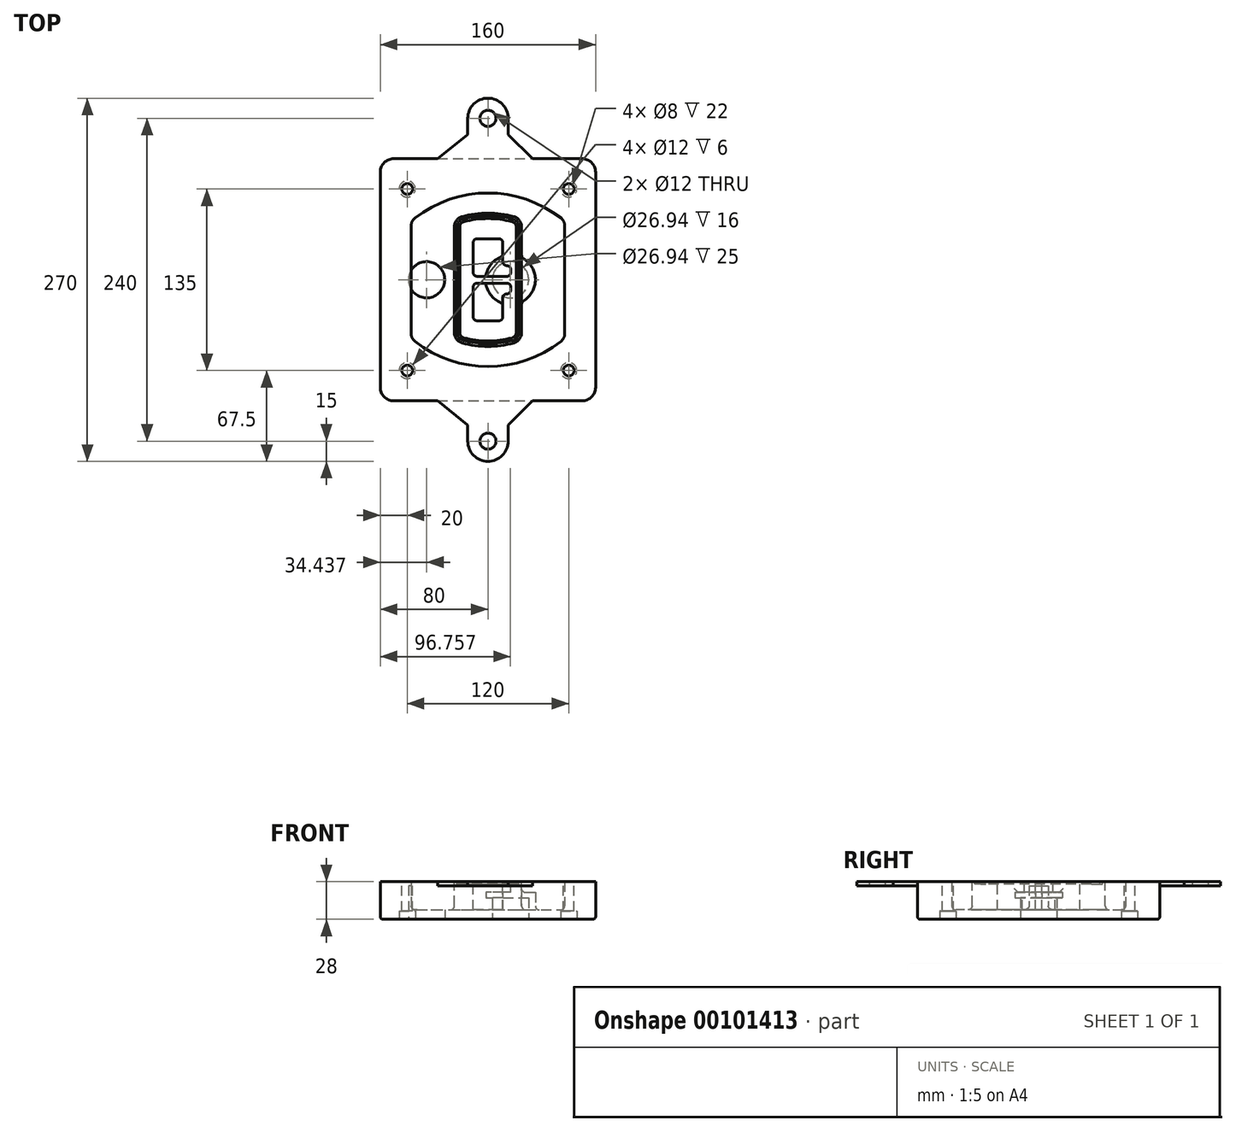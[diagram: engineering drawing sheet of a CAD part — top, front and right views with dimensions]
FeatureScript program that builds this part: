
annotation { "Feature Type Name" : "Feature", "Feature Type Description" : "" }
export const myFeature = defineFeature(function(context is Context, id is Id, definition is map)
    precondition{}
    {
        {
            var Q0;
            Q0=qCreatedBy(makeId("Top.planeOp"),FACE);
            var sketch = newSketch(context, id + "F0", { "sketchPlane" : qUnion([Q0])});
            skPoint(sketch, "E0.rect.middle", {"position": v(0, 0) * mm});
            skLineSegment(sketch, "E1.bottom", {"start": v(-70, -90) * mm, "end": v(70, -90) * mm});
            skLineSegment(sketch, "E1.top", {"start": v(-70, 90) * mm, "end": v(70, 90) * mm});
            skLineSegment(sketch, "E1.left", {"start": v(-80, -80) * mm, "end": v(-80, 80) * mm});
            skLineSegment(sketch, "E1.right", {"start": v(80, -80) * mm, "end": v(80, 80) * mm});
            skLineSegment(sketch, "E2", {"start": v(-80, 90) * mm, "end": v(80, -90) * mm, "construction": true});
            skLineSegment(sketch, "E3", {"start": v(80, 90) * mm, "end": v(-80, -90) * mm, "construction": true});
            skCircle(sketch, "E4", {"center": v(-60, 67.5) * mm, "radius": 4 * mm});
            skCircle(sketch, "E5", {"center": v(60, 67.5) * mm, "radius": 4 * mm});
            skCircle(sketch, "E6", {"center": v(60, -67.5) * mm, "radius": 4 * mm});
            skCircle(sketch, "E7", {"center": v(-60, -67.5) * mm, "radius": 4 * mm});
            skLineSegment(sketch, "E8", {"start": v(-60, 67.5) * mm, "end": v(60, 67.5) * mm, "construction": true});
            skLineSegment(sketch, "E9", {"start": v(60, 67.5) * mm, "end": v(60, -67.5) * mm, "construction": true});
            skLineSegment(sketch, "E10", {"start": v(60, -67.5) * mm, "end": v(-60, -67.5) * mm, "construction": true});
            skLineSegment(sketch, "E11", {"start": v(-60, -67.5) * mm, "end": v(-60, 67.5) * mm, "construction": true});
            skLineSegment(sketch, "E12", {"start": v(-60, 40.3) * mm, "end": v(-60, -40.3) * mm});
            skLineSegment(sketch, "E13", {"start": v(60, 40.3) * mm, "end": v(60, -40.3) * mm});
            skArc(sketch, "E14", {"start": v(56.15, 48.18) * mm, "mid": v(0, 67.5) * mm, "end": v(-56.15, 48.18) * mm});
            skArc(sketch, "E15", {"start": v(-56.15, -48.18) * mm, "mid": v(0, -67.5) * mm, "end": v(56.15, -48.18) * mm});
            skLineSegment(sketch, "E16", {"start": v(-60, 0) * mm, "end": v(60, 0) * mm, "construction": true});
            skPoint(sketch, "E17.visualSharp", {"position": v(-60, -45) * mm});
            skArc(sketch, "E17.filletArc", {"start": v(-60, -40.3) * mm, "mid": v(-58.99, -44.68) * mm, "end": v(-56.15, -48.18) * mm});
            skPoint(sketch, "E18.visualSharp", {"position": v(-60, 45) * mm});
            skArc(sketch, "E18.filletArc", {"start": v(-56.15, 48.18) * mm, "mid": v(-58.99, 44.68) * mm, "end": v(-60, 40.3) * mm});
            skPoint(sketch, "E19.visualSharp", {"position": v(60, 45) * mm});
            skArc(sketch, "E19.filletArc", {"start": v(60, 40.3) * mm, "mid": v(58.99, 44.68) * mm, "end": v(56.15, 48.18) * mm});
            skPoint(sketch, "E20.visualSharp", {"position": v(60, -45) * mm});
            skArc(sketch, "E20.filletArc", {"start": v(56.15, -48.18) * mm, "mid": v(58.99, -44.68) * mm, "end": v(60, -40.3) * mm});
            skPoint(sketch, "E21.visualSharp", {"position": v(-80, 90) * mm});
            skArc(sketch, "E21.filletArc", {"start": v(-70, 90) * mm, "mid": v(-77.07, 87.07) * mm, "end": v(-80, 80) * mm});
            skPoint(sketch, "E22.visualSharp", {"position": v(80, 90) * mm});
            skArc(sketch, "E22.filletArc", {"start": v(80, 80) * mm, "mid": v(77.07, 87.07) * mm, "end": v(70, 90) * mm});
            skPoint(sketch, "E23.visualSharp", {"position": v(80, -90) * mm});
            skArc(sketch, "E23.filletArc", {"start": v(70, -90) * mm, "mid": v(77.07, -87.07) * mm, "end": v(80, -80) * mm});
            skPoint(sketch, "E24.visualSharp", {"position": v(-80, -90) * mm});
            skArc(sketch, "E24.filletArc", {"start": v(-80, -80) * mm, "mid": v(-77.07, -87.07) * mm, "end": v(-70, -90) * mm});
            skArc(sketch, "E25.0", {"start": v(57, 40.3) * mm, "mid": v(56.3, 43.36) * mm, "end": v(54.3, 45.81) * mm});
            skLineSegment(sketch, "E25.1", {"start": v(57, 40.3) * mm, "end": v(57, -40.3) * mm});
            skArc(sketch, "E25.2", {"start": v(54.3, -45.81) * mm, "mid": v(56.3, -43.36) * mm, "end": v(57, -40.3) * mm});
            skArc(sketch, "E25.3", {"start": v(-54.3, -45.81) * mm, "mid": v(0, -64.5) * mm, "end": v(54.3, -45.81) * mm});
            skArc(sketch, "E25.4", {"start": v(-57, -40.3) * mm, "mid": v(-56.3, -43.36) * mm, "end": v(-54.3, -45.81) * mm});
            skArc(sketch, "E25.5", {"start": v(54.3, 45.81) * mm, "mid": v(0, 64.5) * mm, "end": v(-54.3, 45.81) * mm});
            skLineSegment(sketch, "E25.6", {"start": v(-57, 40.3) * mm, "end": v(-57, -40.3) * mm});
            skArc(sketch, "E25.7", {"start": v(-54.3, 45.81) * mm, "mid": v(-56.3, 43.36) * mm, "end": v(-57, 40.3) * mm});
            skArc(sketch, "E26.0", {"start": v(-58.62, 51.33) * mm, "mid": v(-62.58, 46.43) * mm, "end": v(-64, 40.3) * mm});
            skArc(sketch, "E26.1", {"start": v(58.62, 51.33) * mm, "mid": v(0, 71.5) * mm, "end": v(-58.62, 51.33) * mm});
            skArc(sketch, "E26.2", {"start": v(64, 40.3) * mm, "mid": v(62.58, 46.43) * mm, "end": v(58.62, 51.33) * mm});
            skLineSegment(sketch, "E26.3", {"start": v(64, 40.3) * mm, "end": v(64, -40.3) * mm});
            skArc(sketch, "E26.4", {"start": v(58.62, -51.33) * mm, "mid": v(62.58, -46.43) * mm, "end": v(64, -40.3) * mm});
            skLineSegment(sketch, "E26.5", {"start": v(-64, 40.3) * mm, "end": v(-64, -40.3) * mm});
            skArc(sketch, "E26.6", {"start": v(-58.62, -51.33) * mm, "mid": v(0, -71.5) * mm, "end": v(58.62, -51.33) * mm});
            skArc(sketch, "E26.7", {"start": v(-64, -40.3) * mm, "mid": v(-62.58, -46.43) * mm, "end": v(-58.62, -51.33) * mm});
            skSolve(sketch);
        }
        {
            var Q0;
            Q0=makeQuery(id+"F0.imprint","IMPRINT",FACE,{"disambiguationData":[TD([[makeQuery(id+"F0.imprint","IMPRINT",EDGE,{"derivedFrom":sQuery(id+"F0.wireOp",EDGE,"E1.bottom")}),1.0]])]});
            var Q1;
            Q1=makeQuery(id+"F0.imprint","IMPRINT",FACE,{"disambiguationData":[TD([[makeQuery(id+"F0.imprint","IMPRINT",EDGE,{"derivedFrom":sQuery(id+"F0.wireOp",EDGE,"E12")}),1.0]])]});
            var Q2;
            Q2=makeQuery(id+"F0.imprint","IMPRINT",FACE,{"disambiguationData":[TD([[makeQuery(id+"F0.imprint","IMPRINT",EDGE,{"derivedFrom":sQuery(id+"F0.wireOp",EDGE,"E25.0")}),1.0]])]});
            var Q3;
            Q3=makeQuery(id+"F0.imprint","IMPRINT",FACE,{"disambiguationData":[TD([[makeQuery(id+"F0.imprint","IMPRINT",EDGE,{"derivedFrom":sQuery(id+"F0.wireOp",EDGE,"E12")}),-1.0]])]});
            extrude(context, id + "F1", {"entities" : qUnion([Q0, Q1, Q2, Q3]), "oppositeDirection" : true, "depth" : 25 * mm});
        }
        {
            var Q0;
            Q0=makeQuery(id+"F0.imprint","IMPRINT",FACE,{"disambiguationData":[TD([[makeQuery(id+"F0.imprint","IMPRINT",EDGE,{"derivedFrom":sQuery(id+"F0.wireOp",EDGE,"E12")}),1.0]])]});
            extrude(context, id + "F2", {"entities" : qUnion([Q0]), "operationType" : NewBodyOperationType.ADD, "depth" : 3 * mm});
        }
        {
            var Q0;
            Q0=makeQuery(id+"F0.imprint","IMPRINT",FACE,{"disambiguationData":[TD([[makeQuery(id+"F0.imprint","IMPRINT",EDGE,{"derivedFrom":sQuery(id+"F0.wireOp",EDGE,"E25.0")}),1.0]])]});
            extrude(context, id + "F3", {"entities" : qUnion([Q0]), "operationType" : NewBodyOperationType.REMOVE, "oppositeDirection" : true, "depth" : 18 * mm});
        }
        {
            var Q0;
            Q0=makeQuery(id+"F2.opExtrude","CAP_FACE",FACE,{"disambiguationData":[OSD([sQuery(id+"F0.wireOp",EDGE,"E12"),sQuery(id+"F0.wireOp",EDGE,"E13"),sQuery(id+"F0.wireOp",EDGE,"E14"),sQuery(id+"F0.wireOp",EDGE,"E15"),sQuery(id+"F0.wireOp",EDGE,"E17.filletArc"),sQuery(id+"F0.wireOp",EDGE,"E18.filletArc"),sQuery(id+"F0.wireOp",EDGE,"E19.filletArc"),sQuery(id+"F0.wireOp",EDGE,"E20.filletArc"),sQuery(id+"F0.wireOp",EDGE,"E25.0"),sQuery(id+"F0.wireOp",EDGE,"E25.1"),sQuery(id+"F0.wireOp",EDGE,"E25.2"),sQuery(id+"F0.wireOp",EDGE,"E25.3"),sQuery(id+"F0.wireOp",EDGE,"E25.4"),sQuery(id+"F0.wireOp",EDGE,"E25.5"),sQuery(id+"F0.wireOp",EDGE,"E25.6"),sQuery(id+"F0.wireOp",EDGE,"E25.7")])],"isStart":false});
            var sketch = newSketch(context, id + "F4", { "sketchPlane" : qUnion([Q0])});
            skArc(sketch, "E27.0", {"start": v(-19.08, -46.97) * mm, "mid": v(0, -49.5) * mm, "end": v(19.08, -46.97) * mm});
            skArc(sketch, "E28.0", {"start": v(19.08, 46.97) * mm, "mid": v(0, 49.5) * mm, "end": v(-19.08, 46.97) * mm});
            skLineSegment(sketch, "E29", {"start": v(-25, 39.25) * mm, "end": v(-25, -39.25) * mm});
            skLineSegment(sketch, "E30", {"start": v(25, 39.25) * mm, "end": v(25, -39.25) * mm});
            skLineSegment(sketch, "E31", {"start": v(-25, 45.1) * mm, "end": v(25, 45.1) * mm, "construction": true});
            skLineSegment(sketch, "E32", {"start": v(-25, -45.1) * mm, "end": v(25, -45.1) * mm, "construction": true});
            skPoint(sketch, "E33.visualSharp", {"position": v(-25, 45.1) * mm});
            skArc(sketch, "E33.filletArc", {"start": v(-19.08, 46.97) * mm, "mid": v(-23.35, 44.11) * mm, "end": v(-25, 39.25) * mm});
            skPoint(sketch, "E34.visualSharp", {"position": v(25, 45.1) * mm});
            skArc(sketch, "E34.filletArc", {"start": v(25, 39.25) * mm, "mid": v(23.35, 44.11) * mm, "end": v(19.08, 46.97) * mm});
            skPoint(sketch, "E35.visualSharp", {"position": v(25, -45.1) * mm});
            skArc(sketch, "E35.filletArc", {"start": v(19.08, -46.97) * mm, "mid": v(23.35, -44.11) * mm, "end": v(25, -39.25) * mm});
            skPoint(sketch, "E36.visualSharp", {"position": v(-25, -45.1) * mm});
            skArc(sketch, "E36.filletArc", {"start": v(-25, -39.25) * mm, "mid": v(-23.35, -44.11) * mm, "end": v(-19.08, -46.97) * mm});
            skArc(sketch, "E37.0", {"start": v(54.3, 45.81) * mm, "mid": v(0, 64.5) * mm, "end": v(-54.3, 45.81) * mm});
            skArc(sketch, "E37.1", {"start": v(-54.3, 45.81) * mm, "mid": v(-56.3, 43.36) * mm, "end": v(-57, 40.3) * mm});
            skLineSegment(sketch, "E37.2", {"start": v(-57, 40.3) * mm, "end": v(-57, -40.3) * mm});
            skArc(sketch, "E37.3", {"start": v(-57, -40.3) * mm, "mid": v(-56.3, -43.36) * mm, "end": v(-54.3, -45.81) * mm});
            skArc(sketch, "E37.4", {"start": v(-54.3, -45.81) * mm, "mid": v(0, -64.5) * mm, "end": v(54.3, -45.81) * mm});
            skArc(sketch, "E37.5", {"start": v(54.3, -45.81) * mm, "mid": v(56.3, -43.36) * mm, "end": v(57, -40.3) * mm});
            skLineSegment(sketch, "E37.6", {"start": v(57, 40.3) * mm, "end": v(57, -40.3) * mm});
            skArc(sketch, "E37.7", {"start": v(57, 40.3) * mm, "mid": v(56.3, 43.36) * mm, "end": v(54.3, 45.81) * mm});
            skLineSegment(sketch, "E38.0", {"start": v(23, 39.25) * mm, "end": v(23, -39.25) * mm});
            skArc(sketch, "E38.1", {"start": v(18.56, -45.04) * mm, "mid": v(21.76, -42.9) * mm, "end": v(23, -39.25) * mm});
            skArc(sketch, "E38.2", {"start": v(-18.56, -45.04) * mm, "mid": v(0, -47.5) * mm, "end": v(18.56, -45.04) * mm});
            skArc(sketch, "E38.3", {"start": v(-23, -39.25) * mm, "mid": v(-21.76, -42.9) * mm, "end": v(-18.56, -45.04) * mm});
            skLineSegment(sketch, "E38.4", {"start": v(-23, 39.25) * mm, "end": v(-23, -39.25) * mm});
            skArc(sketch, "E38.5", {"start": v(23, 39.25) * mm, "mid": v(21.76, 42.9) * mm, "end": v(18.56, 45.04) * mm});
            skArc(sketch, "E38.6", {"start": v(-18.56, 45.04) * mm, "mid": v(-21.76, 42.9) * mm, "end": v(-23, 39.25) * mm});
            skArc(sketch, "E38.7", {"start": v(18.56, 45.04) * mm, "mid": v(0, 47.5) * mm, "end": v(-18.56, 45.04) * mm});
            skArc(sketch, "E39.0", {"start": v(21, 39.25) * mm, "mid": v(20.18, 41.68) * mm, "end": v(18.04, 43.1) * mm});
            skLineSegment(sketch, "E39.1", {"start": v(21, 39.25) * mm, "end": v(21, -39.25) * mm});
            skArc(sketch, "E39.2", {"start": v(18.04, -43.1) * mm, "mid": v(20.18, -41.68) * mm, "end": v(21, -39.25) * mm});
            skArc(sketch, "E39.3", {"start": v(-18.04, -43.1) * mm, "mid": v(0, -45.5) * mm, "end": v(18.04, -43.1) * mm});
            skArc(sketch, "E39.4", {"start": v(-21, -39.25) * mm, "mid": v(-20.18, -41.68) * mm, "end": v(-18.04, -43.1) * mm});
            skArc(sketch, "E39.5", {"start": v(18.04, 43.1) * mm, "mid": v(0, 45.5) * mm, "end": v(-18.04, 43.1) * mm});
            skLineSegment(sketch, "E39.6", {"start": v(-21, 39.25) * mm, "end": v(-21, -39.25) * mm});
            skArc(sketch, "E39.7", {"start": v(-18.04, 43.1) * mm, "mid": v(-20.18, 41.68) * mm, "end": v(-21, 39.25) * mm});
            skLineSegment(sketch, "E40", {"start": v(-25, 0) * mm, "end": v(25, 0) * mm, "construction": true});
            skLineSegment(sketch, "E41", {"start": v(-11, 5.5) * mm, "end": v(-11, 27.5) * mm});
            skLineSegment(sketch, "E42", {"start": v(-8, 30.5) * mm, "end": v(8, 30.5) * mm});
            skLineSegment(sketch, "E43", {"start": v(11, 27.5) * mm, "end": v(11, 13.5) * mm});
            skLineSegment(sketch, "E44", {"start": v(14, 10.5) * mm, "end": v(14, 10.5) * mm});
            skLineSegment(sketch, "E45", {"start": v(17, 7.5) * mm, "end": v(17, 5.5) * mm});
            skLineSegment(sketch, "E46", {"start": v(14, 2.5) * mm, "end": v(-8, 2.5) * mm});
            skPoint(sketch, "E47.visualSharp", {"position": v(-11, 30.5) * mm});
            skArc(sketch, "E47.filletArc", {"start": v(-8, 30.5) * mm, "mid": v(-10.12, 29.62) * mm, "end": v(-11, 27.5) * mm});
            skPoint(sketch, "E48.visualSharp", {"position": v(11, 30.5) * mm});
            skArc(sketch, "E48.filletArc", {"start": v(11, 27.5) * mm, "mid": v(10.12, 29.62) * mm, "end": v(8, 30.5) * mm});
            skPoint(sketch, "E49.visualSharp", {"position": v(11, 10.5) * mm});
            skArc(sketch, "E49.filletArc", {"start": v(11, 13.5) * mm, "mid": v(11.88, 11.38) * mm, "end": v(14, 10.5) * mm});
            skPoint(sketch, "E50.visualSharp", {"position": v(17, 10.5) * mm});
            skArc(sketch, "E50.filletArc", {"start": v(17, 7.5) * mm, "mid": v(16.12, 9.62) * mm, "end": v(14, 10.5) * mm});
            skPoint(sketch, "E51.visualSharp", {"position": v(17, 2.5) * mm});
            skArc(sketch, "E51.filletArc", {"start": v(14, 2.5) * mm, "mid": v(16.12, 3.38) * mm, "end": v(17, 5.5) * mm});
            skPoint(sketch, "E52.visualSharp", {"position": v(-11, 2.5) * mm});
            skArc(sketch, "E52.filletArc", {"start": v(-11, 5.5) * mm, "mid": v(-10.12, 3.38) * mm, "end": v(-8, 2.5) * mm});
            skLineSegment(sketch, "E53.0.MirrorCS", {"start": v(14, -2.5) * mm, "end": v(-8, -2.5) * mm});
            skArc(sketch, "E54.0.MirrorCS", {"start": v(-11, -5.5) * mm, "mid": v(-10.12, -3.38) * mm, "end": v(-8, -2.5) * mm});
            skLineSegment(sketch, "E55.0.MirrorCS", {"start": v(-11, -5.5) * mm, "end": v(-11, -27.5) * mm});
            skArc(sketch, "E56.0.MirrorCS", {"start": v(-8, -30.5) * mm, "mid": v(-10.12, -29.62) * mm, "end": v(-11, -27.5) * mm});
            skLineSegment(sketch, "E57.0.MirrorCS", {"start": v(-8, -30.5) * mm, "end": v(8, -30.5) * mm});
            skArc(sketch, "E58.0.MirrorCS", {"start": v(11, -27.5) * mm, "mid": v(10.12, -29.62) * mm, "end": v(8, -30.5) * mm});
            skLineSegment(sketch, "E59.0.MirrorCS", {"start": v(11, -27.5) * mm, "end": v(11, -13.5) * mm});
            skArc(sketch, "E60.0.MirrorCS", {"start": v(11, -13.5) * mm, "mid": v(11.88, -11.38) * mm, "end": v(14, -10.5) * mm});
            skArc(sketch, "E61.0.MirrorCS", {"start": v(17, -7.5) * mm, "mid": v(16.12, -9.62) * mm, "end": v(14, -10.5) * mm});
            skLineSegment(sketch, "E62.0.MirrorCS", {"start": v(17, -7.5) * mm, "end": v(17, -5.5) * mm});
            skArc(sketch, "E63.0.MirrorCS", {"start": v(14, -2.5) * mm, "mid": v(16.12, -3.38) * mm, "end": v(17, -5.5) * mm});
            skSolve(sketch);
        }
        {
            var Q0;
            Q0=makeQuery(id+"F4.imprint","IMPRINT",FACE,{"disambiguationData":[TD([[makeQuery(id+"F4.imprint","IMPRINT",EDGE,{"derivedFrom":sQuery(id+"F4.wireOp",EDGE,"E27.0")}),1.0]])]});
            var Q1;
            Q1=makeQuery(id+"F4.imprint","IMPRINT",FACE,{"disambiguationData":[TD([[makeQuery(id+"F4.imprint","IMPRINT",EDGE,{"derivedFrom":sQuery(id+"F4.wireOp",EDGE,"E38.0")}),-1.0]])]});
            var Q2;
            Q2=makeQuery(id+"F4.imprint","IMPRINT",FACE,{"disambiguationData":[TD([[makeQuery(id+"F4.imprint","IMPRINT",EDGE,{"derivedFrom":sQuery(id+"F4.wireOp",EDGE,"E39.0")}),1.0]])]});
            extrude(context, id + "F5", {"entities" : qUnion([Q0, Q1, Q2]), "operationType" : NewBodyOperationType.ADD, "endBound" : BoundingType.UP_TO_NEXT, "oppositeDirection" : true, "depth" : 25 * mm});
        }
        {
            var Q0;
            Q0=makeQuery(id+"F4.imprint","IMPRINT",FACE,{"disambiguationData":[TD([[makeQuery(id+"F4.imprint","IMPRINT",EDGE,{"derivedFrom":sQuery(id+"F4.wireOp",EDGE,"E38.0")}),-1.0]])]});
            extrude(context, id + "F6", {"entities" : qUnion([Q0]), "operationType" : NewBodyOperationType.REMOVE, "oppositeDirection" : true, "depth" : 2 * mm});
        }
        {
            var Q0;
            Q0=makeQuery(id+"F1.opExtrude","CAP_FACE",FACE,{"disambiguationData":[OSD([sQuery(id+"F0.wireOp",EDGE,"E1.bottom"),sQuery(id+"F0.wireOp",EDGE,"E1.top"),sQuery(id+"F0.wireOp",EDGE,"E1.left"),sQuery(id+"F0.wireOp",EDGE,"E1.right"),sQuery(id+"F0.wireOp",EDGE,"E4"),sQuery(id+"F0.wireOp",EDGE,"E5"),sQuery(id+"F0.wireOp",EDGE,"E6"),sQuery(id+"F0.wireOp",EDGE,"E7"),sQuery(id+"F0.wireOp",EDGE,"E21.filletArc"),sQuery(id+"F0.wireOp",EDGE,"E22.filletArc"),sQuery(id+"F0.wireOp",EDGE,"E23.filletArc"),sQuery(id+"F0.wireOp",EDGE,"E24.filletArc")])],"isStart":false});
            var sketch = newSketch(context, id + "F7", { "sketchPlane" : qUnion([Q0])});
            skCircle(sketch, "E64", {"center": v(16.76, 0) * mm, "radius": 13.47 * mm});
            skCircle(sketch, "E65", {"center": v(-45.56, 0) * mm, "radius": 13.47 * mm});
            skLineSegment(sketch, "E66", {"start": v(80, 0) * mm, "end": v(-80, 0) * mm});
            skCircle(sketch, "E67", {"center": v(16.76, 0) * mm, "radius": 18.47 * mm});
            skCircle(sketch, "E68", {"center": v(60, -67.5) * mm, "radius": 6 * mm});
            skCircle(sketch, "E69", {"center": v(-60, -67.5) * mm, "radius": 6 * mm});
            skCircle(sketch, "E70", {"center": v(-60, 67.5) * mm, "radius": 6 * mm});
            skCircle(sketch, "E71", {"center": v(60, 67.5) * mm, "radius": 6 * mm});
            skSolve(sketch);
        }
        {
            var Q0;
            {var subQ1=sQuery(id+"F7.wireOp",EDGE,"E66");var subQ4=sQuery(id+"F7.wireOp",EDGE,"E64");var subQ6=makeQuery(id+"F7.imprint","INTERSECT",VERTEX,{"disambiguationData":[OD(0.0)],"derivedFrom":[subQ4,subQ1]});Q0=makeQuery(id+"F7.imprint","IMPRINT",FACE,{"disambiguationData":[TD([[makeQuery(id+"F7.imprint","IMPRINT",EDGE,{"disambiguationData":[TD([[subQ6,-1.0]])],"derivedFrom":subQ4}),-1.0]])]});}
            var Q1;
            {var subQ0=sQuery(id+"F7.wireOp",EDGE,"E66");var subQ1=sQuery(id+"F7.wireOp",EDGE,"E64");var subQ3=makeQuery(id+"F7.imprint","INTERSECT",VERTEX,{"disambiguationData":[OD(0.0)],"derivedFrom":[subQ1,subQ0]});Q1=makeQuery(id+"F7.imprint","IMPRINT",FACE,{"disambiguationData":[TD([[makeQuery(id+"F7.imprint","IMPRINT",EDGE,{"disambiguationData":[TD([[subQ3,-1.0]])],"derivedFrom":subQ1}),1.0]])]});}
            var Q2;
            {var subQ0=sQuery(id+"F7.wireOp",EDGE,"E66");var subQ1=sQuery(id+"F7.wireOp",EDGE,"E64");var subQ3=makeQuery(id+"F7.imprint","INTERSECT",VERTEX,{"disambiguationData":[OD(0.0)],"derivedFrom":[subQ1,subQ0]});Q2=makeQuery(id+"F7.imprint","IMPRINT",FACE,{"disambiguationData":[TD([[makeQuery(id+"F7.imprint","IMPRINT",EDGE,{"disambiguationData":[TD([[subQ3,1.0]])],"derivedFrom":subQ1}),1.0]])]});}
            var Q3;
            {var subQ1=sQuery(id+"F7.wireOp",EDGE,"E66");var subQ4=sQuery(id+"F7.wireOp",EDGE,"E64");var subQ6=makeQuery(id+"F7.imprint","INTERSECT",VERTEX,{"disambiguationData":[OD(0.0)],"derivedFrom":[subQ4,subQ1]});Q3=makeQuery(id+"F7.imprint","IMPRINT",FACE,{"disambiguationData":[TD([[makeQuery(id+"F7.imprint","IMPRINT",EDGE,{"disambiguationData":[TD([[subQ6,1.0]])],"derivedFrom":subQ4}),-1.0]])]});}
            extrude(context, id + "F8", {"entities" : qUnion([Q0, Q1, Q2, Q3]), "operationType" : NewBodyOperationType.ADD, "oppositeDirection" : true, "depth" : 20 * mm});
        }
        {
            var Q0;
            {var subQ0=sQuery(id+"F7.wireOp",EDGE,"E66");var subQ1=sQuery(id+"F7.wireOp",EDGE,"E64");var subQ3=makeQuery(id+"F7.imprint","INTERSECT",VERTEX,{"disambiguationData":[OD(0.0)],"derivedFrom":[subQ1,subQ0]});Q0=makeQuery(id+"F7.imprint","IMPRINT",FACE,{"disambiguationData":[TD([[makeQuery(id+"F7.imprint","IMPRINT",EDGE,{"disambiguationData":[TD([[subQ3,-1.0]])],"derivedFrom":subQ1}),1.0]])]});}
            var Q1;
            {var subQ0=sQuery(id+"F7.wireOp",EDGE,"E66");var subQ1=sQuery(id+"F7.wireOp",EDGE,"E64");var subQ3=makeQuery(id+"F7.imprint","INTERSECT",VERTEX,{"disambiguationData":[OD(0.0)],"derivedFrom":[subQ1,subQ0]});Q1=makeQuery(id+"F7.imprint","IMPRINT",FACE,{"disambiguationData":[TD([[makeQuery(id+"F7.imprint","IMPRINT",EDGE,{"disambiguationData":[TD([[subQ3,1.0]])],"derivedFrom":subQ1}),1.0]])]});}
            extrude(context, id + "F9", {"entities" : qUnion([Q0, Q1]), "operationType" : NewBodyOperationType.REMOVE, "oppositeDirection" : true, "depth" : 16 * mm});
        }
        {
            var Q0;
            {var subQ0=sQuery(id+"F7.wireOp",EDGE,"E66");var subQ1=sQuery(id+"F7.wireOp",EDGE,"E65");var subQ3=makeQuery(id+"F7.imprint","INTERSECT",VERTEX,{"disambiguationData":[OD(0.0)],"derivedFrom":[subQ1,subQ0]});Q0=makeQuery(id+"F7.imprint","IMPRINT",FACE,{"disambiguationData":[TD([[makeQuery(id+"F7.imprint","IMPRINT",EDGE,{"disambiguationData":[TD([[subQ3,-1.0]])],"derivedFrom":subQ1}),1.0]])]});}
            var Q1;
            {var subQ0=sQuery(id+"F7.wireOp",EDGE,"E66");var subQ1=sQuery(id+"F7.wireOp",EDGE,"E65");var subQ3=makeQuery(id+"F7.imprint","INTERSECT",VERTEX,{"disambiguationData":[OD(0.0)],"derivedFrom":[subQ1,subQ0]});Q1=makeQuery(id+"F7.imprint","IMPRINT",FACE,{"disambiguationData":[TD([[makeQuery(id+"F7.imprint","IMPRINT",EDGE,{"disambiguationData":[TD([[subQ3,1.0]])],"derivedFrom":subQ1}),1.0]])]});}
            extrude(context, id + "F10", {"entities" : qUnion([Q0, Q1]), "operationType" : NewBodyOperationType.REMOVE, "oppositeDirection" : true, "depth" : 25 * mm});
        }
        {
            var Q0;
            Q0=makeQuery(id+"F7.imprint","IMPRINT",FACE,{"disambiguationData":[TD([[makeQuery(id+"F7.imprint","IMPRINT",EDGE,{"derivedFrom":sQuery(id+"F7.wireOp",EDGE,"E68")}),1.0]])]});
            var Q1;
            Q1=makeQuery(id+"F7.imprint","IMPRINT",FACE,{"disambiguationData":[TD([[makeQuery(id+"F7.imprint","IMPRINT",EDGE,{"derivedFrom":makeQuery(id+"F1.opExtrude","CAP_EDGE",EDGE,{"disambiguationData":[OSD([sQuery(id+"F0.wireOp",EDGE,"E5")])],"isStart":false})}),-1.0]])]});
            var Q2;
            Q2=makeQuery(id+"F7.imprint","IMPRINT",FACE,{"disambiguationData":[TD([[makeQuery(id+"F7.imprint","IMPRINT",EDGE,{"derivedFrom":sQuery(id+"F7.wireOp",EDGE,"E69")}),1.0]])]});
            var Q3;
            Q3=makeQuery(id+"F7.imprint","IMPRINT",FACE,{"disambiguationData":[TD([[makeQuery(id+"F7.imprint","IMPRINT",EDGE,{"derivedFrom":makeQuery(id+"F1.opExtrude","CAP_EDGE",EDGE,{"disambiguationData":[OSD([sQuery(id+"F0.wireOp",EDGE,"E4")])],"isStart":false})}),-1.0]])]});
            var Q4;
            Q4=makeQuery(id+"F7.imprint","IMPRINT",FACE,{"disambiguationData":[TD([[makeQuery(id+"F7.imprint","IMPRINT",EDGE,{"derivedFrom":sQuery(id+"F7.wireOp",EDGE,"E70")}),1.0]])]});
            var Q5;
            Q5=makeQuery(id+"F7.imprint","IMPRINT",FACE,{"disambiguationData":[TD([[makeQuery(id+"F7.imprint","IMPRINT",EDGE,{"derivedFrom":makeQuery(id+"F1.opExtrude","CAP_EDGE",EDGE,{"disambiguationData":[OSD([sQuery(id+"F0.wireOp",EDGE,"E7")])],"isStart":false})}),-1.0]])]});
            var Q6;
            Q6=makeQuery(id+"F7.imprint","IMPRINT",FACE,{"disambiguationData":[TD([[makeQuery(id+"F7.imprint","IMPRINT",EDGE,{"derivedFrom":sQuery(id+"F7.wireOp",EDGE,"E71")}),1.0]])]});
            var Q7;
            Q7=makeQuery(id+"F7.imprint","IMPRINT",FACE,{"disambiguationData":[TD([[makeQuery(id+"F7.imprint","IMPRINT",EDGE,{"derivedFrom":makeQuery(id+"F1.opExtrude","CAP_EDGE",EDGE,{"disambiguationData":[OSD([sQuery(id+"F0.wireOp",EDGE,"E6")])],"isStart":false})}),-1.0]])]});
            extrude(context, id + "F11", {"entities" : qUnion([Q0, Q1, Q2, Q3, Q4, Q5, Q6, Q7]), "operationType" : NewBodyOperationType.REMOVE, "oppositeDirection" : true, "depth" : 6 * mm});
        }
        {
            var Q0;
            Q0=makeQuery(id+"F9.boolean.opBoolean","COPY",FACE,{"derivedFrom":makeQuery(id+"F9.opExtrude","CAP_FACE",FACE,{"disambiguationData":[OSD([sQuery(id+"F7.wireOp",EDGE,"E64")])],"isStart":false})});
            var sketch = newSketch(context, id + "F12", { "sketchPlane" : qUnion([Q0])});
            skArc(sketch, "E72.0", {"start": v(11, 17.55) * mm, "mid": v(2.57, 11.82) * mm, "end": v(-1.54, 2.5) * mm});
            skArc(sketch, "E72.1", {"start": v(-1.54, -2.5) * mm, "mid": v(2.57, -11.82) * mm, "end": v(11, -17.55) * mm});
            skLineSegment(sketch, "E73", {"start": v(-1.54, -2.5) * mm, "end": v(14, -2.5) * mm});
            skLineSegment(sketch, "E74.0", {"start": v(14, 2.5) * mm, "end": v(-1.54, 2.5) * mm});
            skArc(sketch, "E74.1", {"start": v(14, 2.5) * mm, "mid": v(16.12, 3.38) * mm, "end": v(17, 5.5) * mm});
            skLineSegment(sketch, "E74.2", {"start": v(17, 7.5) * mm, "end": v(17, 5.5) * mm});
            skArc(sketch, "E74.3", {"start": v(17, 7.5) * mm, "mid": v(16.12, 9.62) * mm, "end": v(14, 10.5) * mm});
            skArc(sketch, "E74.4", {"start": v(11, 13.5) * mm, "mid": v(11.88, 11.38) * mm, "end": v(14, 10.5) * mm});
            skLineSegment(sketch, "E74.5", {"start": v(11, 17.55) * mm, "end": v(11, 13.5) * mm});
            skLineSegment(sketch, "E74.7", {"start": v(14, -2.5) * mm, "end": v(-1.54, -2.5) * mm});
            skArc(sketch, "E74.8", {"start": v(14, -2.5) * mm, "mid": v(16.12, -3.38) * mm, "end": v(17, -5.5) * mm});
            skLineSegment(sketch, "E74.9", {"start": v(17, -7.5) * mm, "end": v(17, -5.5) * mm});
            skArc(sketch, "E74.10", {"start": v(17, -7.5) * mm, "mid": v(16.12, -9.62) * mm, "end": v(14, -10.5) * mm});
            skArc(sketch, "E74.11", {"start": v(11, -13.5) * mm, "mid": v(11.88, -11.38) * mm, "end": v(14, -10.5) * mm});
            skLineSegment(sketch, "E74.12", {"start": v(11, -17.55) * mm, "end": v(11, -13.5) * mm});
            skPoint(sketch, "E75.orphan", {"position": v(11, -27.5) * mm});
            skPoint(sketch, "E76.orphan", {"position": v(-8, -2.5) * mm});
            skPoint(sketch, "E77.orphan", {"position": v(-8, 2.5) * mm});
            skPoint(sketch, "E78.orphan", {"position": v(11, 27.5) * mm});
            skSolve(sketch);
        }
        {
            var Q0;
            {var subQ7=sQuery(id+"F12.wireOp",EDGE,"E72.0");var subQ14=sQuery(id+"F12.wireOp",EDGE,"E72.1");var subQ16=sQuery(id+"F12.wireOp",EDGE,"E74.1");var subQ18=sQuery(id+"F12.wireOp",EDGE,"E74.8");Q0=qUnion([makeQuery(id+"F12.imprint","IMPRINT",FACE,{"disambiguationData":[TD([[makeQuery(id+"F12.imprint","IMPRINT",EDGE,{"derivedFrom":subQ7}),1.0]])]}),makeQuery(id+"F12.imprint","IMPRINT",FACE,{"disambiguationData":[TD([[makeQuery(id+"F12.imprint","IMPRINT",EDGE,{"derivedFrom":subQ14}),1.0]])]}),makeQuery(id+"F12.imprint","IMPRINT",FACE,{"disambiguationData":[TD([[makeQuery(id+"F12.imprint","IMPRINT",EDGE,{"derivedFrom":subQ16}),1.0]])]}),makeQuery(id+"F12.imprint","IMPRINT",FACE,{"disambiguationData":[TD([[makeQuery(id+"F12.imprint","IMPRINT",EDGE,{"derivedFrom":subQ18}),-1.0]])]})]);}
            var Q1;
            Q1=makeQuery(id+"F5.boolean.opBoolean","SPLIT",FACE,{"disambiguationData":[TD([makeQuery(id+"F5.opExtrude","SWEPT_FACE",FACE,{"disambiguationData":[OSD([sQuery(id+"F4.wireOp",EDGE,"E41")])]})])],"derivedFrom":makeQuery(id+"F3.boolean.opBoolean","COPY",FACE,{"derivedFrom":makeQuery(id+"F3.opExtrude","CAP_FACE",FACE,{"disambiguationData":[OSD([sQuery(id+"F0.wireOp",EDGE,"E25.0"),sQuery(id+"F0.wireOp",EDGE,"E25.1"),sQuery(id+"F0.wireOp",EDGE,"E25.2"),sQuery(id+"F0.wireOp",EDGE,"E25.3"),sQuery(id+"F0.wireOp",EDGE,"E25.4"),sQuery(id+"F0.wireOp",EDGE,"E25.5"),sQuery(id+"F0.wireOp",EDGE,"E25.6"),sQuery(id+"F0.wireOp",EDGE,"E25.7")])],"isStart":false})})});
            extrude(context, id + "F13", {"entities" : qUnion([Q0]), "operationType" : NewBodyOperationType.REMOVE, "endBound" : BoundingType.UP_TO_SURFACE, "endBoundEntityFace" : qUnion([Q1]), "depth" : 25 * mm});
        }
        {
            var Q0;
            Q0=makeQuery(id+"F3.boolean.opBoolean","COPY",EDGE,{"derivedFrom":makeQuery(id+"F3.opExtrude","CAP_EDGE",EDGE,{"disambiguationData":[OSD([sQuery(id+"F0.wireOp",EDGE,"E25.6")])],"isStart":false})});
            var Q1;
            Q1=makeQuery(id+"F8.boolean.opBoolean","INTERSECT",EDGE,{"derivedFrom":[makeQuery(id+"F5.opExtrude","SWEPT_FACE",FACE,{"disambiguationData":[OSD([sQuery(id+"F4.wireOp",EDGE,"E30")])]}),makeQuery(id+"F8.opExtrude","CAP_FACE",FACE,{"disambiguationData":[OSD([sQuery(id+"F7.wireOp",EDGE,"E67")])],"isStart":false})]});
            var Q2;
            Q2=makeQuery(id+"F8.boolean.opBoolean","INTERSECT",EDGE,{"disambiguationData":[OD(1.0)],"derivedFrom":[makeQuery(id+"F5.opExtrude","SWEPT_FACE",FACE,{"disambiguationData":[OSD([sQuery(id+"F4.wireOp",EDGE,"E30")])]}),makeQuery(id+"F8.opExtrude","SWEPT_FACE",FACE,{"disambiguationData":[OSD([sQuery(id+"F7.wireOp",EDGE,"E67")])]})]});
            var Q3;
            {var subQ0=sQuery(id+"F4.wireOp",EDGE,"E30");Q3=makeQuery(id+"F8.boolean.opBoolean","SPLIT",EDGE,{"disambiguationData":[TD([makeQuery(id+"F5.opExtrude","SWEPT_FACE",FACE,{"disambiguationData":[OSD([sQuery(id+"F4.wireOp",EDGE,"E35.filletArc")])]})])],"derivedFrom":makeQuery(id+"F5.opExtrude","CAP_EDGE",EDGE,{"disambiguationData":[OSD([subQ0])],"isStart":false})});}
            var Q4;
            {var subQ0=sQuery(id+"F0.wireOp",EDGE,"E25.7");var subQ1=sQuery(id+"F0.wireOp",EDGE,"E25.1");var subQ2=sQuery(id+"F0.wireOp",EDGE,"E25.6");var subQ3=sQuery(id+"F0.wireOp",EDGE,"E25.5");var subQ4=sQuery(id+"F0.wireOp",EDGE,"E25.4");var subQ5=sQuery(id+"F0.wireOp",EDGE,"E25.0");var subQ6=sQuery(id+"F0.wireOp",EDGE,"E25.2");var subQ7=sQuery(id+"F0.wireOp",EDGE,"E25.3");Q4=makeQuery(id+"F8.boolean.opBoolean","INTERSECT",EDGE,{"derivedFrom":[makeQuery(id+"F5.boolean.opBoolean","SPLIT",FACE,{"disambiguationData":[TD([makeQuery(id+"F2.opExtrude","SWEPT_FACE",FACE,{"disambiguationData":[OSD([subQ5])]})])],"derivedFrom":makeQuery(id+"F3.boolean.opBoolean","COPY",FACE,{"derivedFrom":makeQuery(id+"F3.opExtrude","CAP_FACE",FACE,{"disambiguationData":[OSD([subQ5,subQ1,subQ6,subQ7,subQ4,subQ3,subQ2,subQ0])],"isStart":false})})}),makeQuery(id+"F8.opExtrude","SWEPT_FACE",FACE,{"disambiguationData":[OSD([sQuery(id+"F7.wireOp",EDGE,"E67")])]})]});}
            var Q5;
            Q5=makeQuery(id+"F8.boolean.opBoolean","INTERSECT",EDGE,{"disambiguationData":[OD(0.0)],"derivedFrom":[makeQuery(id+"F5.opExtrude","SWEPT_FACE",FACE,{"disambiguationData":[OSD([sQuery(id+"F4.wireOp",EDGE,"E30")])]}),makeQuery(id+"F8.opExtrude","SWEPT_FACE",FACE,{"disambiguationData":[OSD([sQuery(id+"F7.wireOp",EDGE,"E67")])]})]});
            fillet(context, id + "F14", {"entities" : qUnion([Q0, Q1, Q2, Q3, Q4, Q5]), "radius" : 3 * mm, "tangentPropagation" : true, "allowEdgeOverflow" : false});
        }
        {
            var Q0;
            Q0=makeQuery(id+"F1.opExtrude","CAP_EDGE",EDGE,{"disambiguationData":[OSD([sQuery(id+"F0.wireOp",EDGE,"E1.bottom")])],"isStart":false});
            fillet(context, id + "F15", {"entities" : qUnion([Q0]), "radius" : 2 * mm, "tangentPropagation" : true, "allowEdgeOverflow" : false});
        }
        {
            var Q0;
            {var subQ0=sQuery(id+"F0.wireOp",EDGE,"E22.filletArc");var subQ1=sQuery(id+"F0.wireOp",EDGE,"E7");var subQ2=sQuery(id+"F0.wireOp",EDGE,"E6");var subQ3=sQuery(id+"F0.wireOp",EDGE,"E5");var subQ4=sQuery(id+"F0.wireOp",EDGE,"E4");var subQ5=sQuery(id+"F0.wireOp",EDGE,"E1.bottom");var subQ6=sQuery(id+"F0.wireOp",EDGE,"E21.filletArc");var subQ7=sQuery(id+"F0.wireOp",EDGE,"E1.top");var subQ8=sQuery(id+"F0.wireOp",EDGE,"E1.left");var subQ9=sQuery(id+"F0.wireOp",EDGE,"E1.right");var subQ10=sQuery(id+"F0.wireOp",EDGE,"E23.filletArc");var subQ11=sQuery(id+"F0.wireOp",EDGE,"E24.filletArc");Q0=makeQuery(id+"F2.boolean.opBoolean","SPLIT",FACE,{"disambiguationData":[TD([makeQuery(id+"F1.opExtrude","SWEPT_FACE",FACE,{"disambiguationData":[OSD([subQ5])]})])],"derivedFrom":makeQuery(id+"F1.opExtrude","CAP_FACE",FACE,{"disambiguationData":[OSD([subQ5,subQ7,subQ8,subQ9,subQ4,subQ3,subQ2,subQ1,subQ6,subQ0,subQ10,subQ11])],"isStart":true})});}
            var sketch = newSketch(context, id + "F16", { "sketchPlane" : qUnion([Q0])});
            skLineSegment(sketch, "E79.0", {"start": v(-80, -80) * mm, "end": v(-80, 80) * mm});
            skArc(sketch, "E79.1", {"start": v(-70, 90) * mm, "mid": v(-77.07, 87.07) * mm, "end": v(-80, 80) * mm});
            skLineSegment(sketch, "E79.2", {"start": v(-70, 90) * mm, "end": v(70, 90) * mm});
            skCircle(sketch, "E79.3", {"center": v(-60, 67.5) * mm, "radius": 4 * mm});
            skArc(sketch, "E79.4", {"start": v(-56.15, 48.18) * mm, "mid": v(-58.99, 44.68) * mm, "end": v(-60, 40.3) * mm});
            skArc(sketch, "E79.5", {"start": v(56.15, 48.18) * mm, "mid": v(0, 67.5) * mm, "end": v(-56.15, 48.18) * mm});
            skCircle(sketch, "E79.6", {"center": v(60, 67.5) * mm, "radius": 4 * mm});
            skArc(sketch, "E79.7", {"start": v(80, 80) * mm, "mid": v(77.07, 87.07) * mm, "end": v(70, 90) * mm});
            skLineSegment(sketch, "E79.8", {"start": v(80, -80) * mm, "end": v(80, 80) * mm});
            skArc(sketch, "E79.9", {"start": v(60, 40.3) * mm, "mid": v(58.99, 44.68) * mm, "end": v(56.15, 48.18) * mm});
            skLineSegment(sketch, "E79.10", {"start": v(60, 40.3) * mm, "end": v(60, -40.3) * mm});
            skArc(sketch, "E79.11", {"start": v(56.15, -48.18) * mm, "mid": v(58.99, -44.68) * mm, "end": v(60, -40.3) * mm});
            skArc(sketch, "E79.12", {"start": v(-56.15, -48.18) * mm, "mid": v(0, -67.5) * mm, "end": v(56.15, -48.18) * mm});
            skArc(sketch, "E79.13", {"start": v(70, -90) * mm, "mid": v(77.07, -87.07) * mm, "end": v(80, -80) * mm});
            skLineSegment(sketch, "E79.14", {"start": v(-70, -90) * mm, "end": v(70, -90) * mm});
            skCircle(sketch, "E79.15", {"center": v(60, -67.5) * mm, "radius": 4 * mm});
            skCircle(sketch, "E79.16", {"center": v(-60, -67.5) * mm, "radius": 4 * mm});
            skArc(sketch, "E79.17", {"start": v(-80, -80) * mm, "mid": v(-77.07, -87.07) * mm, "end": v(-70, -90) * mm});
            skArc(sketch, "E79.18", {"start": v(-60, -40.3) * mm, "mid": v(-58.99, -44.68) * mm, "end": v(-56.15, -48.18) * mm});
            skLineSegment(sketch, "E79.19", {"start": v(-60, 40.3) * mm, "end": v(-60, -40.3) * mm});
            skLineSegment(sketch, "E80", {"start": v(0, 90) * mm, "end": v(0, 120) * mm, "construction": true});
            skCircle(sketch, "E81", {"center": v(0, 120) * mm, "radius": 6 * mm});
            skArc(sketch, "E82", {"start": v(15, 120) * mm, "mid": v(0, 135) * mm, "end": v(-15, 120) * mm});
            skLineSegment(sketch, "E83", {"start": v(-15, 120) * mm, "end": v(-15, 108) * mm});
            skLineSegment(sketch, "E84", {"start": v(-15, 108) * mm, "end": v(-37.5, 90) * mm});
            skLineSegment(sketch, "E85", {"start": v(15, 120) * mm, "end": v(15, 108) * mm});
            skLineSegment(sketch, "E86", {"start": v(15, 108) * mm, "end": v(33, 90) * mm});
            skLineSegment(sketch, "E87", {"start": v(-80, 0) * mm, "end": v(80, 0) * mm, "construction": true});
            skLineSegment(sketch, "E88.MirrorCS", {"start": v(15, -108) * mm, "end": v(33, -90) * mm});
            skLineSegment(sketch, "E89.MirrorCS", {"start": v(15, -120) * mm, "end": v(15, -108) * mm});
            skCircle(sketch, "E90.MirrorC", {"center": v(0, -120) * mm, "radius": 6 * mm});
            skLineSegment(sketch, "E91.MirrorCS", {"start": v(-15, -120) * mm, "end": v(-15, -108) * mm});
            skLineSegment(sketch, "E92.MirrorCS", {"start": v(-15, -108) * mm, "end": v(-37.5, -90) * mm});
            skLineSegment(sketch, "E93.MirrorCS", {"start": v(0, -90) * mm, "end": v(0, -120) * mm, "construction": true});
            skArc(sketch, "E94.MirrorCS", {"start": v(15, -120) * mm, "mid": v(0, -135) * mm, "end": v(-15, -120) * mm});
            skSolve(sketch);
        }
        {
            var Q0;
            Q0 = qSketchRegion(id + "F16", true);
            var Q1;
            Q1=makeQuery(id+"F2.opExtrude","CAP_FACE",FACE,{"disambiguationData":[OSD([sQuery(id+"F0.wireOp",EDGE,"E12"),sQuery(id+"F0.wireOp",EDGE,"E13"),sQuery(id+"F0.wireOp",EDGE,"E14"),sQuery(id+"F0.wireOp",EDGE,"E15"),sQuery(id+"F0.wireOp",EDGE,"E17.filletArc"),sQuery(id+"F0.wireOp",EDGE,"E18.filletArc"),sQuery(id+"F0.wireOp",EDGE,"E19.filletArc"),sQuery(id+"F0.wireOp",EDGE,"E20.filletArc"),sQuery(id+"F0.wireOp",EDGE,"E25.0"),sQuery(id+"F0.wireOp",EDGE,"E25.1"),sQuery(id+"F0.wireOp",EDGE,"E25.2"),sQuery(id+"F0.wireOp",EDGE,"E25.3"),sQuery(id+"F0.wireOp",EDGE,"E25.4"),sQuery(id+"F0.wireOp",EDGE,"E25.5"),sQuery(id+"F0.wireOp",EDGE,"E25.6"),sQuery(id+"F0.wireOp",EDGE,"E25.7")])],"isStart":false});
            extrude(context, id + "F17", {"entities" : qUnion([Q0]), "operationType" : NewBodyOperationType.ADD, "endBound" : BoundingType.UP_TO_SURFACE, "endBoundEntityFace" : qUnion([Q1]), "depth" : 25 * mm});
        }
    });
